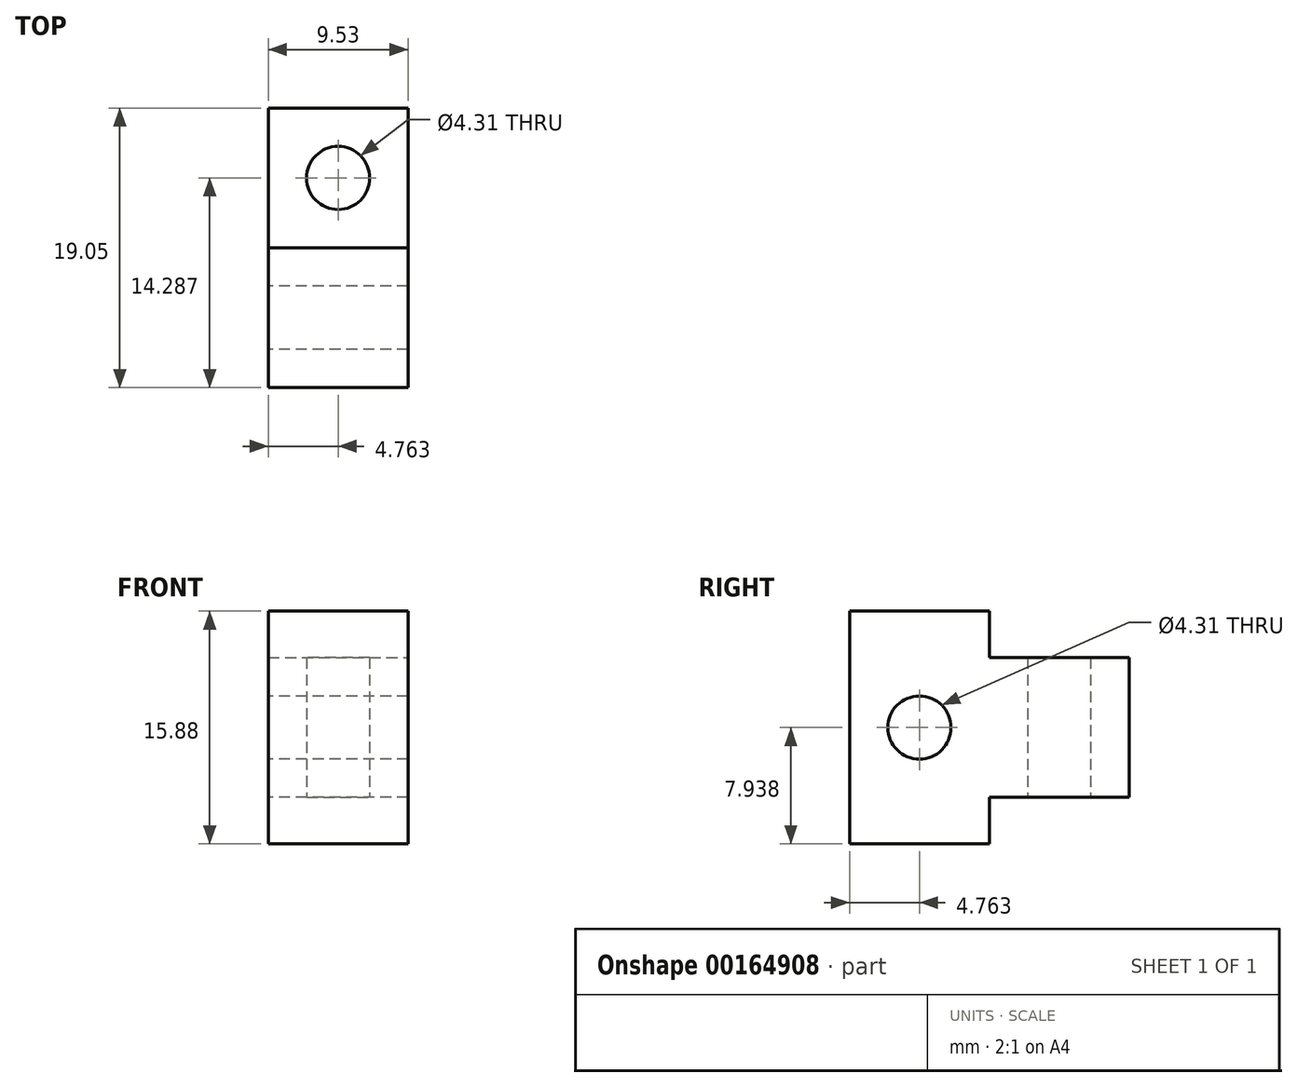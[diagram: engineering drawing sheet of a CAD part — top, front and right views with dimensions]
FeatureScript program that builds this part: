
annotation { "Feature Type Name" : "Feature", "Feature Type Description" : "" }
export const myFeature = defineFeature(function(context is Context, id is Id, definition is map)
    precondition{}
    {
        {
            var Q0;
            Q0=qCreatedBy(makeId("Top.planeOp"),FACE);
            var sketch = newSketch(context, id + "F0", { "sketchPlane" : qUnion([Q0])});
            skLineSegment(sketch, "E0.bottom", {"start": v(0, 0) * mm, "end": v(9.53, 0) * mm});
            skLineSegment(sketch, "E0.top", {"start": v(0, 19.05) * mm, "end": v(9.52, 19.05) * mm});
            skLineSegment(sketch, "E0.left", {"start": v(0, 0) * mm, "end": v(0, 19.05) * mm});
            skLineSegment(sketch, "E0.right", {"start": v(9.53, 0) * mm, "end": v(9.52, 19.05) * mm});
            skLineSegment(sketch, "E1", {"start": v(4.76, 19.05) * mm, "end": v(4.76, 14.29) * mm, "construction": true});
            skLineSegment(sketch, "E2", {"start": v(4.76, 14.29) * mm, "end": v(9.53, 14.29) * mm, "construction": true});
            skCircle(sketch, "E3", {"center": v(4.76, 14.29) * mm, "radius": 2.15 * mm});
            skSolve(sketch);
        }
        {
            var Q0;
            Q0 = qSketchRegion(id + "F0", true);
            extrude(context, id + "F1", {"entities" : qUnion([Q0]), "depth" : 15.88 * mm});
        }
        {
            var Q0;
            Q0=makeQuery(id+"F1.opExtrude","SWEPT_FACE",FACE,{"disambiguationData":[OSD([sQuery(id+"F0.wireOp",EDGE,"E0.top")])]});
            var sketch = newSketch(context, id + "F2", { "sketchPlane" : qUnion([Q0])});
            skLineSegment(sketch, "E4.bottom", {"start": v(-9.52, 0) * mm, "end": v(0, 0) * mm});
            skLineSegment(sketch, "E4.top", {"start": v(-9.52, 3.18) * mm, "end": v(0, 3.18) * mm});
            skLineSegment(sketch, "E4.left", {"start": v(-9.52, 0) * mm, "end": v(-9.52, 3.18) * mm});
            skLineSegment(sketch, "E4.right", {"start": v(0, 0) * mm, "end": v(0, 3.18) * mm});
            skLineSegment(sketch, "E5.bottom", {"start": v(0, 15.88) * mm, "end": v(-9.53, 15.88) * mm});
            skLineSegment(sketch, "E5.top", {"start": v(0, 12.7) * mm, "end": v(-9.52, 12.7) * mm});
            skLineSegment(sketch, "E5.left", {"start": v(0, 15.88) * mm, "end": v(0, 12.7) * mm});
            skLineSegment(sketch, "E5.right", {"start": v(-9.52, 15.88) * mm, "end": v(-9.52, 12.7) * mm});
            skSolve(sketch);
        }
        {
            var Q0;
            Q0 = qSketchRegion(id + "F2", true);
            extrude(context, id + "F3", {"entities" : qUnion([Q0]), "operationType" : NewBodyOperationType.REMOVE, "oppositeDirection" : true, "depth" : 9.52 * mm});
        }
        {
            var Q0;
            Q0=makeQuery(id+"F1.opExtrude","SWEPT_FACE",FACE,{"disambiguationData":[OSD([sQuery(id+"F0.wireOp",EDGE,"E0.left")])]});
            var sketch = newSketch(context, id + "F4", { "sketchPlane" : qUnion([Q0])});
            skLineSegment(sketch, "E6", {"start": v(-4.76, 0) * mm, "end": v(-4.76, 15.88) * mm, "construction": true});
            skCircle(sketch, "E7", {"center": v(-4.76, 7.94) * mm, "radius": 2.15 * mm});
            skSolve(sketch);
        }
        {
            var Q0;
            Q0 = qSketchRegion(id + "F4", true);
            var Q1;
            Q1=makeQuery(id+"F1.opExtrude","SWEPT_FACE",FACE,{"disambiguationData":[OSD([sQuery(id+"F0.wireOp",EDGE,"E0.right")])]});
            extrude(context, id + "F5", {"entities" : qUnion([Q0]), "operationType" : NewBodyOperationType.REMOVE, "endBound" : BoundingType.UP_TO_SURFACE, "oppositeDirection" : true, "endBoundEntityFace" : qUnion([Q1]), "depth" : 6.35 * mm});
        }
    });
